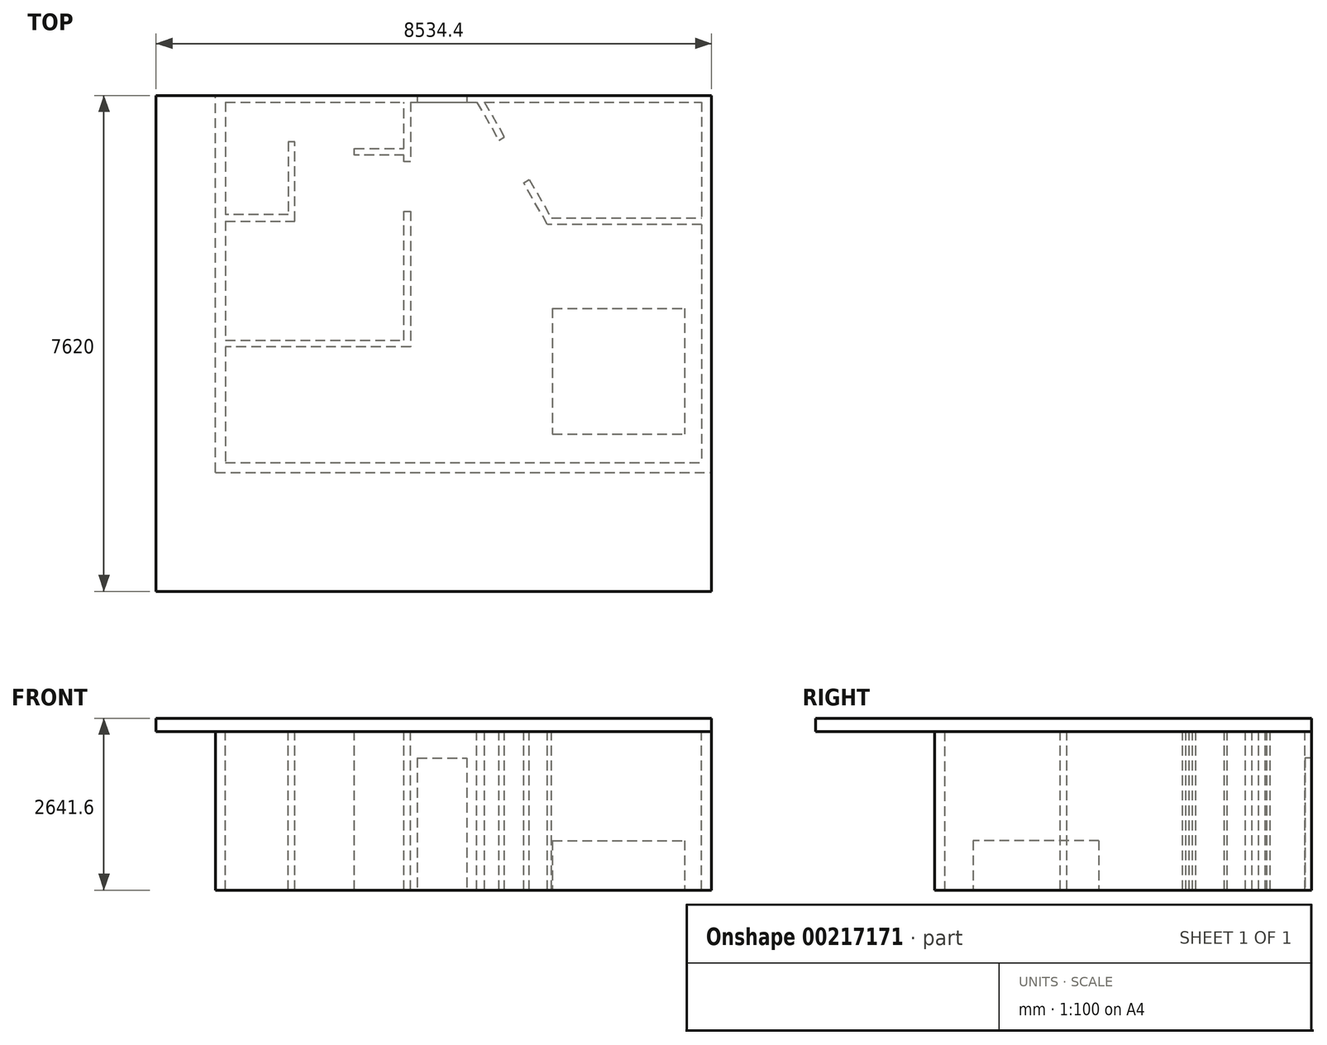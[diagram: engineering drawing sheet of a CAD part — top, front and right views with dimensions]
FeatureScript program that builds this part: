
annotation { "Feature Type Name" : "Feature", "Feature Type Description" : "" }
export const myFeature = defineFeature(function(context is Context, id is Id, definition is map)
    precondition{}
    {
        {
            var Q0;
            Q0=qCreatedBy(makeId("Top.planeOp"),FACE);
            var sketch = newSketch(context, id + "F0", { "sketchPlane" : qUnion([Q0])});
            skLineSegment(sketch, "E0.bottom", {"start": v(0, 0) * mm, "end": v(7620, 0) * mm});
            skLineSegment(sketch, "E0.top", {"start": v(0, 5791.2) * mm, "end": v(7620, 5791.2) * mm});
            skLineSegment(sketch, "E0.left", {"start": v(0, 0) * mm, "end": v(0, 5791.2) * mm});
            skLineSegment(sketch, "E0.right", {"start": v(7620, 0) * mm, "end": v(7620, 5791.2) * mm});
            skLineSegment(sketch, "E1.top", {"start": v(152.4, 152.4) * mm, "end": v(7467.6, 152.4) * mm});
            skLineSegment(sketch, "E1.right", {"start": v(7467.6, 5689.6) * mm, "end": v(7467.6, 152.4) * mm});
            skLineSegment(sketch, "E2", {"start": v(152.4, 5689.6) * mm, "end": v(7467.6, 5689.6) * mm});
            skLineSegment(sketch, "E3", {"start": v(152.4, 5689.6) * mm, "end": v(152.4, 152.4) * mm});
            skSolve(sketch);
        }
        {
            var Q0;
            Q0 = qSketchRegion(id + "F0", true);
            extrude(context, id + "F1", {"entities" : qUnion([Q0]), "depth" : 2438.4 * mm});
        }
        {
            var Q0;
            Q0=makeQuery(id+"F1.opExtrude","SWEPT_FACE",FACE,{"disambiguationData":[OSD([sQuery(id+"F0.wireOp",EDGE,"E2")])]});
            var sketch = newSketch(context, id + "F2", { "sketchPlane" : qUnion([Q0])});
            skLineSegment(sketch, "E4.bottom", {"start": v(3098.8, 2032) * mm, "end": v(3860.8, 2032) * mm});
            skLineSegment(sketch, "E4.top", {"start": v(3098.8, 0) * mm, "end": v(3860.8, 0) * mm});
            skLineSegment(sketch, "E4.left", {"start": v(3098.8, 2032) * mm, "end": v(3098.8, 0) * mm});
            skLineSegment(sketch, "E4.right", {"start": v(3860.8, 2032) * mm, "end": v(3860.8, 0) * mm});
            skSolve(sketch);
        }
        {
            var Q0;
            Q0 = qSketchRegion(id + "F2", true);
            extrude(context, id + "F3", {"entities" : qUnion([Q0]), "operationType" : NewBodyOperationType.REMOVE, "endBound" : BoundingType.UP_TO_NEXT, "oppositeDirection" : true, "depth" : 25.4 * mm});
        }
        {
            var Q0;
            Q0=makeQuery(id+"F1.opExtrude","CAP_FACE",FACE,{"disambiguationData":[OSD([sQuery(id+"F0.wireOp",EDGE,"E0.bottom"),sQuery(id+"F0.wireOp",EDGE,"E0.top"),sQuery(id+"F0.wireOp",EDGE,"E0.left"),sQuery(id+"F0.wireOp",EDGE,"E0.right"),sQuery(id+"F0.wireOp",EDGE,"E1.top"),sQuery(id+"F0.wireOp",EDGE,"E1.right"),sQuery(id+"F0.wireOp",EDGE,"E2"),sQuery(id+"F0.wireOp",EDGE,"E3")])],"isStart":false});
            var sketch = newSketch(context, id + "F4", { "sketchPlane" : qUnion([Q0])});
            skLineSegment(sketch, "E5", {"start": v(2997.2, 5689.6) * mm, "end": v(2997.2, 4775.2) * mm});
            skLineSegment(sketch, "E6", {"start": v(2997.2, 4775.2) * mm, "end": v(2895.6, 4775.2) * mm});
            skLineSegment(sketch, "E7", {"start": v(2895.6, 4775.2) * mm, "end": v(2895.6, 4876.8) * mm});
            skLineSegment(sketch, "E8", {"start": v(2895.6, 4876.8) * mm, "end": v(2133.6, 4876.8) * mm});
            skLineSegment(sketch, "E9", {"start": v(2133.6, 4876.8) * mm, "end": v(2133.6, 4978.4) * mm});
            skLineSegment(sketch, "E10", {"start": v(2133.6, 4978.4) * mm, "end": v(2895.6, 4978.4) * mm});
            skLineSegment(sketch, "E11", {"start": v(2895.6, 4978.4) * mm, "end": v(2895.6, 5689.6) * mm});
            skLineSegment(sketch, "E12", {"start": v(2895.6, 5689.6) * mm, "end": v(2997.2, 5689.6) * mm});
            skLineSegment(sketch, "E13", {"start": v(152.4, 2032) * mm, "end": v(2895.6, 2032) * mm});
            skLineSegment(sketch, "E14", {"start": v(2895.6, 2032) * mm, "end": v(2895.6, 4013.2) * mm});
            skLineSegment(sketch, "E15", {"start": v(2895.6, 4013.2) * mm, "end": v(2997.2, 4013.2) * mm});
            skLineSegment(sketch, "E16", {"start": v(2997.2, 4013.2) * mm, "end": v(2997.2, 1930.4) * mm});
            skLineSegment(sketch, "E17", {"start": v(2997.2, 1930.4) * mm, "end": v(152.4, 1930.4) * mm});
            skLineSegment(sketch, "E18", {"start": v(152.4, 1930.4) * mm, "end": v(152.4, 2032) * mm});
            skLineSegment(sketch, "E19", {"start": v(152.4, 3860.8) * mm, "end": v(1219.2, 3860.8) * mm});
            skLineSegment(sketch, "E20", {"start": v(1219.2, 3860.8) * mm, "end": v(1219.2, 5080) * mm});
            skLineSegment(sketch, "E21", {"start": v(1219.2, 5080) * mm, "end": v(1117.6, 5080) * mm});
            skLineSegment(sketch, "E22", {"start": v(1117.6, 5080) * mm, "end": v(1117.6, 3962.4) * mm});
            skLineSegment(sketch, "E23", {"start": v(1117.6, 3962.4) * mm, "end": v(152.4, 3962.4) * mm});
            skLineSegment(sketch, "E24", {"start": v(152.4, 3962.4) * mm, "end": v(152.4, 3860.8) * mm});
            skLineSegment(sketch, "E25", {"start": v(4013.2, 5689.6) * mm, "end": v(4350.63, 5105.16) * mm});
            skLineSegment(sketch, "E26", {"start": v(4350.63, 5105.16) * mm, "end": v(4438.62, 5155.96) * mm});
            skLineSegment(sketch, "E27", {"start": v(4438.62, 5155.96) * mm, "end": v(4130.52, 5689.6) * mm});
            skLineSegment(sketch, "E28", {"start": v(4130.52, 5689.6) * mm, "end": v(4013.2, 5689.6) * mm});
            skLineSegment(sketch, "E29", {"start": v(7467.6, 3810) * mm, "end": v(5098.39, 3810) * mm});
            skLineSegment(sketch, "E30", {"start": v(5098.39, 3810) * mm, "end": v(4731.63, 4445.24) * mm});
            skLineSegment(sketch, "E31", {"start": v(4731.63, 4445.24) * mm, "end": v(4819.62, 4496.04) * mm});
            skLineSegment(sketch, "E32", {"start": v(4819.62, 4496.04) * mm, "end": v(5157.05, 3911.6) * mm});
            skLineSegment(sketch, "E33", {"start": v(5157.05, 3911.6) * mm, "end": v(7467.6, 3911.6) * mm});
            skLineSegment(sketch, "E34", {"start": v(7467.6, 3911.6) * mm, "end": v(7467.6, 3810) * mm});
            skLineSegment(sketch, "E35", {"start": v(4775.62, 4470.64) * mm, "end": v(4394.62, 5130.56) * mm, "construction": true});
            skLineSegment(sketch, "E36", {"start": v(4585.12, 4800.6) * mm, "end": v(7467.6, 4800.6) * mm, "construction": true});
            skLineSegment(sketch, "E37", {"start": v(6247.83, 5689.6) * mm, "end": v(6247.83, 4800.6) * mm, "construction": true});
            skLineSegment(sketch, "E38", {"start": v(6247.83, 4800.6) * mm, "end": v(6247.83, 3911.6) * mm, "construction": true});
            skSolve(sketch);
        }
        {
            var Q0;
            Q0 = qSketchRegion(id + "F4", true);
            var Q1;
            Q1=makeQuery(id+"F1.opExtrude","CAP_FACE",FACE,{"disambiguationData":[OSD([sQuery(id+"F0.wireOp",EDGE,"E0.bottom"),sQuery(id+"F0.wireOp",EDGE,"E0.top"),sQuery(id+"F0.wireOp",EDGE,"E0.left"),sQuery(id+"F0.wireOp",EDGE,"E0.right"),sQuery(id+"F0.wireOp",EDGE,"E1.top"),sQuery(id+"F0.wireOp",EDGE,"E1.right"),sQuery(id+"F0.wireOp",EDGE,"E2"),sQuery(id+"F0.wireOp",EDGE,"E3")])],"isStart":true});
            extrude(context, id + "F5", {"entities" : qUnion([Q0]), "operationType" : NewBodyOperationType.ADD, "endBound" : BoundingType.UP_TO_SURFACE, "oppositeDirection" : true, "endBoundEntityFace" : qUnion([Q1]), "depth" : 25.4 * mm});
        }
        {
            var Q0;
            Q0=qCreatedBy(makeId("Top.planeOp"),FACE);
            var sketch = newSketch(context, id + "F6", { "sketchPlane" : qUnion([Q0])});
            skLineSegment(sketch, "E39.bottom", {"start": v(5174.2, 2521.06) * mm, "end": v(7206.2, 2521.06) * mm});
            skLineSegment(sketch, "E39.top", {"start": v(5174.2, 590.66) * mm, "end": v(7206.2, 590.66) * mm});
            skLineSegment(sketch, "E39.left", {"start": v(5174.2, 2521.06) * mm, "end": v(5174.2, 590.66) * mm});
            skLineSegment(sketch, "E39.right", {"start": v(7206.2, 2521.06) * mm, "end": v(7206.2, 590.66) * mm});
            skSolve(sketch);
        }
        {
            var Q0;
            Q0 = qSketchRegion(id + "F6", true);
            extrude(context, id + "F7", {"entities" : qUnion([Q0]), "depth" : 762 * mm});
        }
        {
            var Q0;
            Q0=makeQuery(id+"F5.boolean.opBoolean","MERGE",FACE,{"derivedFrom":[makeQuery(id+"F1.opExtrude","CAP_FACE",FACE,{"disambiguationData":[OSD([sQuery(id+"F0.wireOp",EDGE,"E0.bottom"),sQuery(id+"F0.wireOp",EDGE,"E0.top"),sQuery(id+"F0.wireOp",EDGE,"E0.left"),sQuery(id+"F0.wireOp",EDGE,"E0.right"),sQuery(id+"F0.wireOp",EDGE,"E1.top"),sQuery(id+"F0.wireOp",EDGE,"E1.right"),sQuery(id+"F0.wireOp",EDGE,"E2"),sQuery(id+"F0.wireOp",EDGE,"E3")])],"isStart":false}),makeQuery(id+"F5.opExtrude","CAP_FACE",FACE,{"disambiguationData":[OSD([sQuery(id+"F4.wireOp",EDGE,"E5"),sQuery(id+"F4.wireOp",EDGE,"E6"),sQuery(id+"F4.wireOp",EDGE,"E7"),sQuery(id+"F4.wireOp",EDGE,"E8"),sQuery(id+"F4.wireOp",EDGE,"E9"),sQuery(id+"F4.wireOp",EDGE,"E10"),sQuery(id+"F4.wireOp",EDGE,"E11"),sQuery(id+"F4.wireOp",EDGE,"E12")])],"isStart":true}),makeQuery(id+"F5.opExtrude","CAP_FACE",FACE,{"disambiguationData":[OSD([sQuery(id+"F4.wireOp",EDGE,"E13"),sQuery(id+"F4.wireOp",EDGE,"E14"),sQuery(id+"F4.wireOp",EDGE,"E15"),sQuery(id+"F4.wireOp",EDGE,"E16"),sQuery(id+"F4.wireOp",EDGE,"E17"),sQuery(id+"F4.wireOp",EDGE,"E18")])],"isStart":true}),makeQuery(id+"F5.opExtrude","CAP_FACE",FACE,{"disambiguationData":[OSD([sQuery(id+"F4.wireOp",EDGE,"E19"),sQuery(id+"F4.wireOp",EDGE,"E20"),sQuery(id+"F4.wireOp",EDGE,"E21"),sQuery(id+"F4.wireOp",EDGE,"E22"),sQuery(id+"F4.wireOp",EDGE,"E23"),sQuery(id+"F4.wireOp",EDGE,"E24")])],"isStart":true}),makeQuery(id+"F5.opExtrude","CAP_FACE",FACE,{"disambiguationData":[OSD([sQuery(id+"F4.wireOp",EDGE,"E25"),sQuery(id+"F4.wireOp",EDGE,"E26"),sQuery(id+"F4.wireOp",EDGE,"E27"),sQuery(id+"F4.wireOp",EDGE,"E28")])],"isStart":true}),makeQuery(id+"F5.opExtrude","CAP_FACE",FACE,{"disambiguationData":[OSD([sQuery(id+"F4.wireOp",EDGE,"E29"),sQuery(id+"F4.wireOp",EDGE,"E30"),sQuery(id+"F4.wireOp",EDGE,"E31"),sQuery(id+"F4.wireOp",EDGE,"E32"),sQuery(id+"F4.wireOp",EDGE,"E33"),sQuery(id+"F4.wireOp",EDGE,"E34")])],"isStart":true})]});
            var sketch = newSketch(context, id + "F8", { "sketchPlane" : qUnion([Q0])});
            skLineSegment(sketch, "E40.bottom", {"start": v(7620, 5791.2) * mm, "end": v(-914.4, 5791.2) * mm});
            skLineSegment(sketch, "E40.top", {"start": v(7620, -1828.8) * mm, "end": v(-914.4, -1828.8) * mm});
            skLineSegment(sketch, "E40.left", {"start": v(7620, 5791.2) * mm, "end": v(7620, -1828.8) * mm});
            skLineSegment(sketch, "E40.right", {"start": v(-914.4, 5791.2) * mm, "end": v(-914.4, -1828.8) * mm});
            skSolve(sketch);
        }
        {
            var Q0;
            Q0 = qSketchRegion(id + "F8", true);
            extrude(context, id + "F9", {"entities" : qUnion([Q0]), "depth" : 203.2 * mm});
        }
    });
